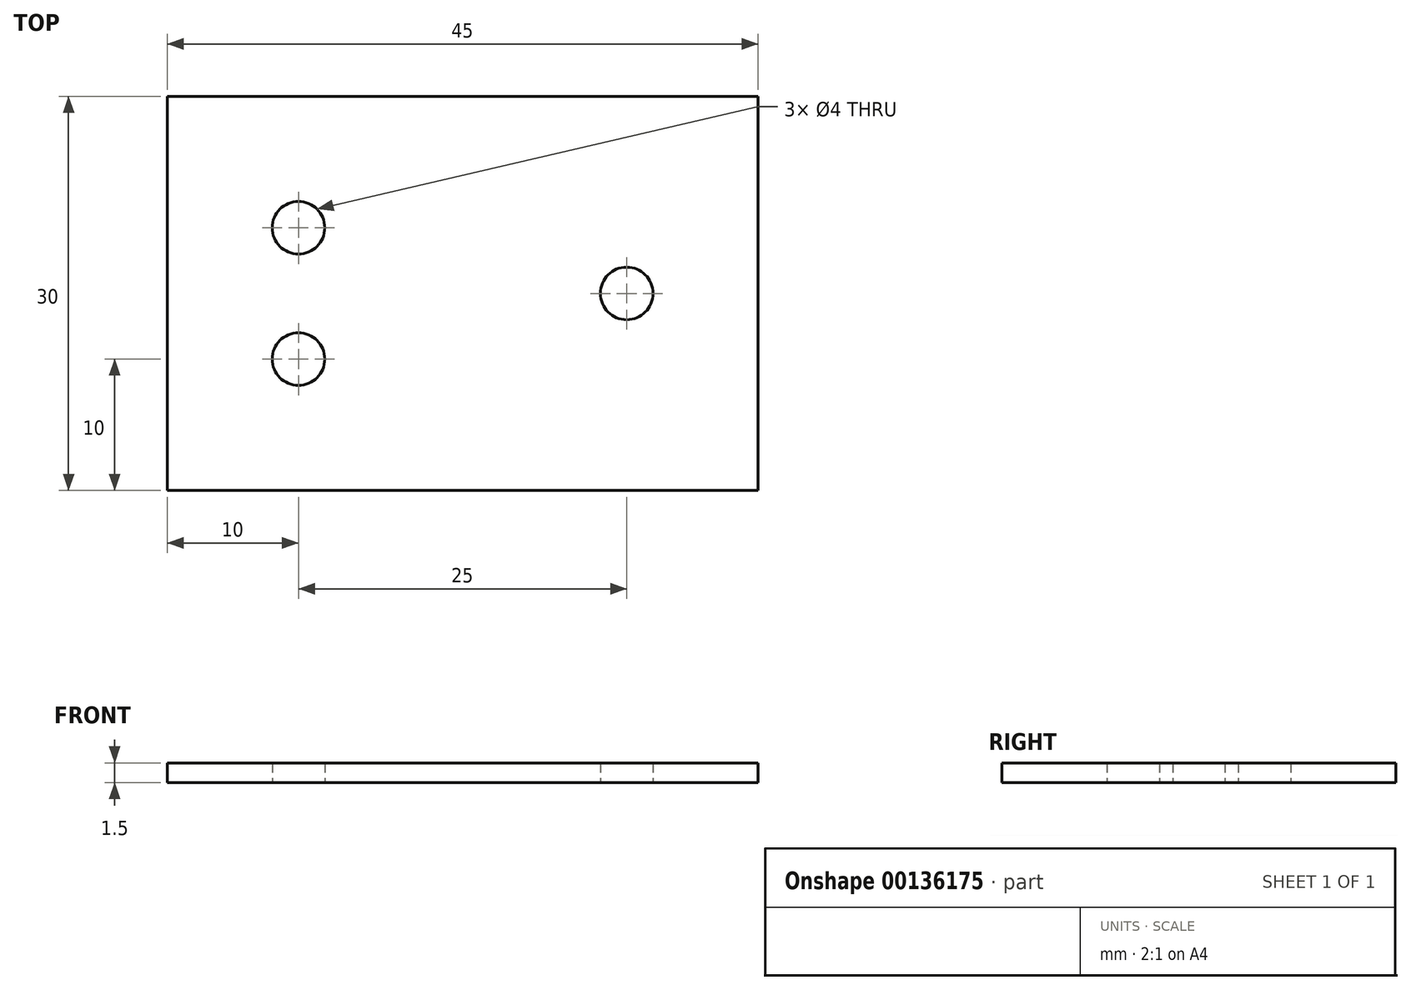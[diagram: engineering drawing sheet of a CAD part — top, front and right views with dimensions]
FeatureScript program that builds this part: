
annotation { "Feature Type Name" : "Feature", "Feature Type Description" : "" }
export const myFeature = defineFeature(function(context is Context, id is Id, definition is map)
    precondition{}
    {
        {
            var Q0;
            Q0=qCreatedBy(makeId("Top.planeOp"),FACE);
            var sketch = newSketch(context, id + "F0", { "sketchPlane" : qUnion([Q0])});
            skLineSegment(sketch, "E0.bottom", {"start": v(0, 0) * mm, "end": v(-45, 0) * mm});
            skLineSegment(sketch, "E0.top", {"start": v(0, 30) * mm, "end": v(-45, 30) * mm});
            skLineSegment(sketch, "E0.left", {"start": v(0, 0) * mm, "end": v(0, 30) * mm});
            skLineSegment(sketch, "E0.right", {"start": v(-45, 0) * mm, "end": v(-45, 30) * mm});
            skCircle(sketch, "E1", {"center": v(-35, 20) * mm, "radius": 2 * mm});
            skCircle(sketch, "E2", {"center": v(-35, 10) * mm, "radius": 2 * mm});
            skCircle(sketch, "E3", {"center": v(-10, 15) * mm, "radius": 2 * mm});
            skSolve(sketch);
        }
        {
            var Q0;
            Q0 = qSketchRegion(id + "F0", true);
            extrude(context, id + "F1", {"entities" : qUnion([Q0]), "depth" : 1.5 * mm});
        }
    });
